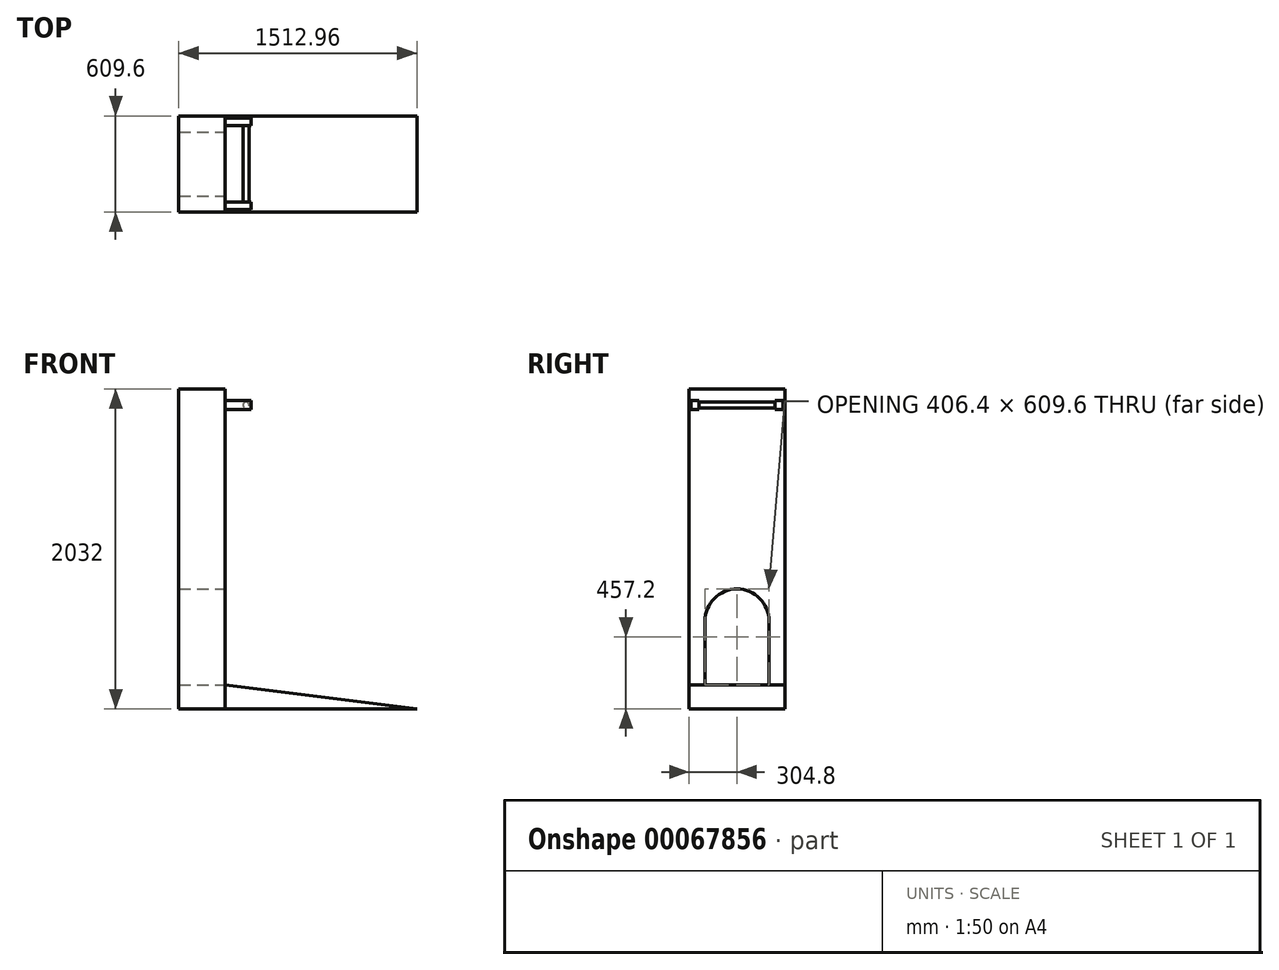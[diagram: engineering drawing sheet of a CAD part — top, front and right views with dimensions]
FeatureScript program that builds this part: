
annotation { "Feature Type Name" : "Feature", "Feature Type Description" : "" }
export const myFeature = defineFeature(function(context is Context, id is Id, definition is map)
    precondition{}
    {
        {
            var Q0;
            Q0=qCreatedBy(makeId("Front.planeOp"),FACE);
            var sketch = newSketch(context, id + "F0", { "sketchPlane" : qUnion([Q0])});
            skLineSegment(sketch, "E0", {"start": v(0, 0) * mm, "end": v(-1219.2, 0) * mm});
            skLineSegment(sketch, "E1", {"start": v(-1219.2, 0) * mm, "end": v(-1219.2, 152.4) * mm});
            skLineSegment(sketch, "E2", {"start": v(-1219.2, 152.4) * mm, "end": v(0, 0) * mm});
            skSolve(sketch);
        }
        {
            var Q0;
            Q0=makeQuery(id+"F0.imprint","IMPRINT",FACE,{"disambiguationData":[TD([[makeQuery(id+"F0.imprint","IMPRINT",EDGE,{"derivedFrom":sQuery(id+"F0.wireOp",EDGE,"E0")}),-1.0]])]});
            extrude(context, id + "F1", {"entities" : qUnion([Q0]), "depth" : 609.6 * mm});
        }
        {
            var Q0;
            Q0=makeQuery(id+"F1.opExtrude","SWEPT_FACE",FACE,{"disambiguationData":[OSD([sQuery(id+"F0.wireOp",EDGE,"E0")])]});
            var sketch = newSketch(context, id + "F2", { "sketchPlane" : qUnion([Q0])});
            skLineSegment(sketch, "E3.bottom", {"start": v(-1219.2, 609.6) * mm, "end": v(-1512.96, 609.6) * mm});
            skLineSegment(sketch, "E3.top", {"start": v(-1219.2, 0) * mm, "end": v(-1512.96, 0) * mm});
            skLineSegment(sketch, "E3.left", {"start": v(-1219.2, 609.6) * mm, "end": v(-1219.2, 0) * mm});
            skLineSegment(sketch, "E3.right", {"start": v(-1512.96, 609.6) * mm, "end": v(-1512.96, 0) * mm});
            skSolve(sketch);
        }
        {
            var Q0;
            Q0 = qSketchRegion(id + "F2", true);
            extrude(context, id + "F3", {"entities" : qUnion([Q0]), "oppositeDirection" : true, "depth" : 2032 * mm});
        }
        {
            var Q0;
            Q0=makeQuery(id+"F3.opExtrude","SWEPT_FACE",FACE,{"disambiguationData":[OSD([sQuery(id+"F2.wireOp",EDGE,"E3.left")])]});
            var sketch = newSketch(context, id + "F4", { "sketchPlane" : qUnion([Q0])});
            skLineSegment(sketch, "E4.bottom", {"start": v(-596.08, 1902.3) * mm, "end": v(-546.92, 1902.3) * mm});
            skLineSegment(sketch, "E4.top", {"start": v(-596.08, 1958.5) * mm, "end": v(-546.92, 1958.5) * mm});
            skLineSegment(sketch, "E4.left", {"start": v(-596.08, 1958.5) * mm, "end": v(-596.08, 1902.3) * mm});
            skLineSegment(sketch, "E4.right", {"start": v(-546.92, 1958.5) * mm, "end": v(-546.92, 1902.3) * mm});
            skLineSegment(sketch, "E5", {"start": v(-304.8, 2032) * mm, "end": v(-304.8, 1268.99) * mm, "construction": true});
            skLineSegment(sketch, "E6.MirrorCS", {"start": v(-13.52, 1902.3) * mm, "end": v(-62.68, 1902.3) * mm});
            skLineSegment(sketch, "E7.MirrorCS", {"start": v(-13.52, 1958.5) * mm, "end": v(-62.68, 1958.5) * mm});
            skLineSegment(sketch, "E8.MirrorCS", {"start": v(-62.68, 1958.5) * mm, "end": v(-62.68, 1902.3) * mm});
            skLineSegment(sketch, "E9.MirrorCS", {"start": v(-13.52, 1958.5) * mm, "end": v(-13.52, 1902.3) * mm});
            skPoint(sketch, "E10", {"position": v(-571.5, 1902.3) * mm});
            skPoint(sketch, "E11", {"position": v(-38.1, 1902.3) * mm});
            skPoint(sketch, "E12", {"position": v(-62.68, 1930.4) * mm});
            skSolve(sketch);
        }
        {
            var Q0;
            Q0 = qSketchRegion(id + "F4", true);
            extrude(context, id + "F5", {"entities" : qUnion([Q0]), "operationType" : NewBodyOperationType.ADD, "depth" : 165.1 * mm});
        }
        {
            var Q0;
            Q0=makeQuery(id+"F5.opExtrude","SWEPT_FACE",FACE,{"disambiguationData":[OSD([sQuery(id+"F4.wireOp",EDGE,"E4.right")])]});
            var sketch = newSketch(context, id + "F6", { "sketchPlane" : qUnion([Q0])});
            skLineSegment(sketch, "E13", {"start": v(1054.1, 1930.4) * mm, "end": v(1219.2, 1930.4) * mm, "construction": true});
            skCircle(sketch, "E14", {"center": v(1085.85, 1930.4) * mm, "radius": 19.05 * mm});
            skSolve(sketch);
        }
        {
            var Q0;
            Q0=makeQuery(id+"F6.imprint","IMPRINT",FACE,{"disambiguationData":[TD([[makeQuery(id+"F6.imprint","IMPRINT",EDGE,{"derivedFrom":sQuery(id+"F6.wireOp",EDGE,"E14")}),1.0]])]});
            extrude(context, id + "F7", {"entities" : qUnion([Q0]), "operationType" : NewBodyOperationType.ADD, "endBound" : BoundingType.UP_TO_NEXT, "depth" : 25.4 * mm});
        }
        {
            var Q0;
            Q0=makeQuery(id+"F3.opExtrude","SWEPT_FACE",FACE,{"disambiguationData":[OSD([sQuery(id+"F2.wireOp",EDGE,"E3.left")])]});
            var sketch = newSketch(context, id + "F8", { "sketchPlane" : qUnion([Q0])});
            skLineSegment(sketch, "E15", {"start": v(-508, 152.4) * mm, "end": v(-508, 558.8) * mm});
            skLineSegment(sketch, "E16", {"start": v(-101.6, 152.4) * mm, "end": v(-101.6, 558.8) * mm});
            skArc(sketch, "E17", {"start": v(-508, 558.8) * mm, "mid": v(-304.8, 762) * mm, "end": v(-101.6, 558.8) * mm});
            skPoint(sketch, "E18", {"position": v(-304.8, 762) * mm});
            skLineSegment(sketch, "E19", {"start": v(-304.8, 558.8) * mm, "end": v(-304.8, 152.4) * mm, "construction": true});
            skLineSegment(sketch, "E20", {"start": v(-508, 152.4) * mm, "end": v(-101.6, 152.4) * mm});
            skSolve(sketch);
        }
        {
            var Q0;
            Q0=makeQuery(id+"F8.imprint","IMPRINT",FACE,{"disambiguationData":[TD([[makeQuery(id+"F8.imprint","IMPRINT",EDGE,{"derivedFrom":sQuery(id+"F8.wireOp",EDGE,"E15")}),-1.0]])]});
            extrude(context, id + "F9", {"entities" : qUnion([Q0]), "operationType" : NewBodyOperationType.REMOVE, "endBound" : BoundingType.UP_TO_NEXT, "oppositeDirection" : true, "depth" : 25.4 * mm});
        }
    });
